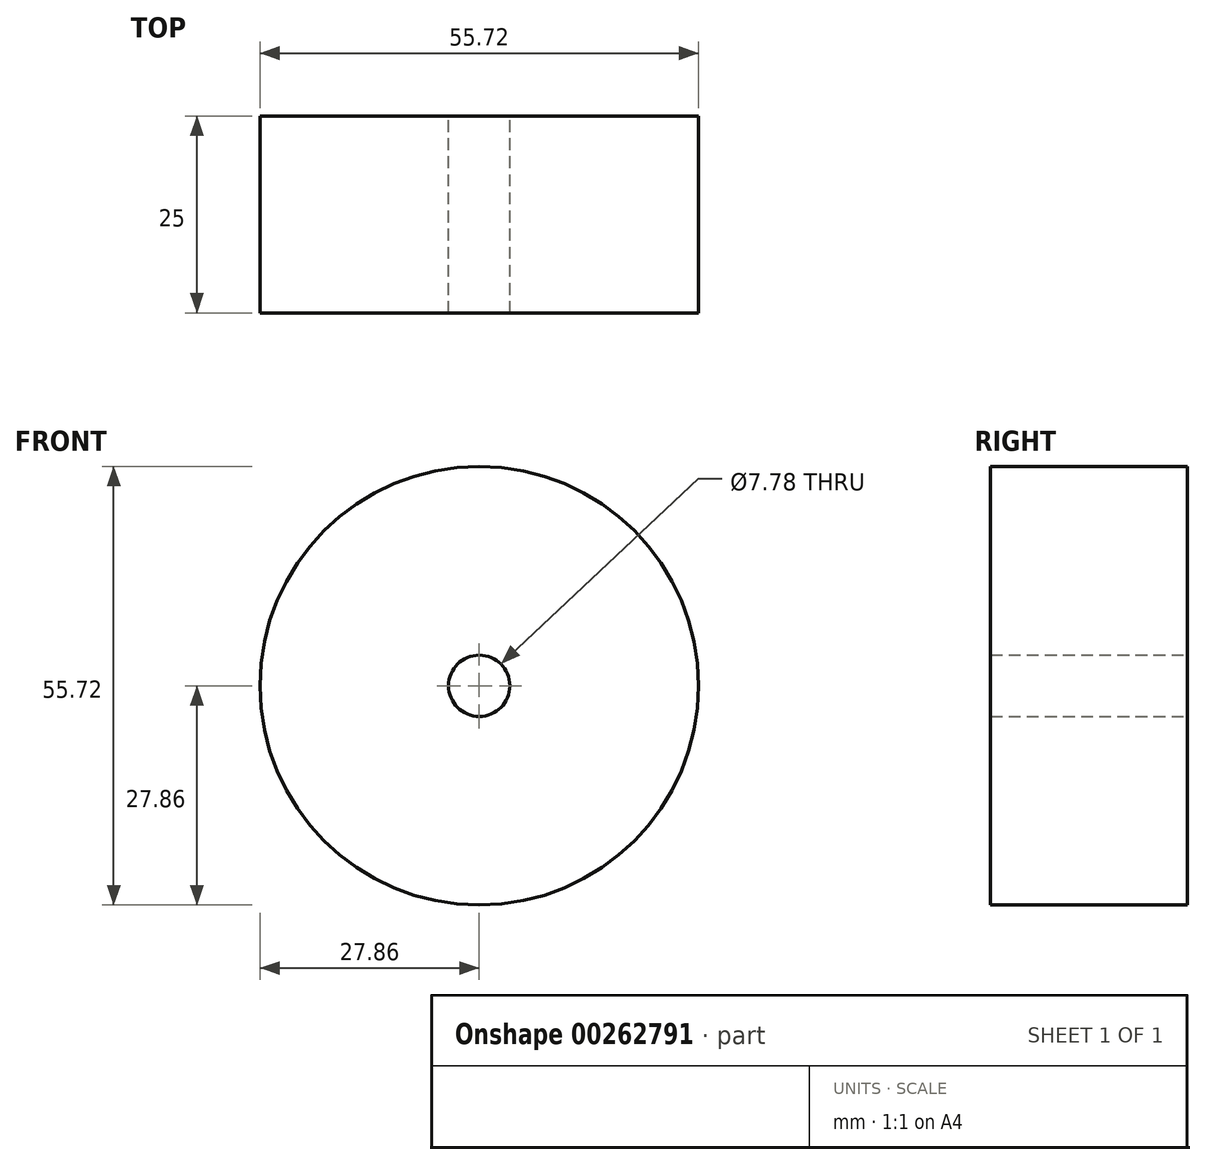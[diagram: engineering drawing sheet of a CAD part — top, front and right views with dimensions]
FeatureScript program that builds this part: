
annotation { "Feature Type Name" : "Feature", "Feature Type Description" : "" }
export const myFeature = defineFeature(function(context is Context, id is Id, definition is map)
    precondition{}
    {
        {
            var Q0;
            Q0=qCreatedBy(makeId("Front.planeOp"),FACE);
            var sketch = newSketch(context, id + "F0", { "sketchPlane" : qUnion([Q0])});
            skCircle(sketch, "E0", {"center": v(0, 0) * mm, "radius": 27.86 * mm});
            skCircle(sketch, "E1", {"center": v(0, 0) * mm, "radius": 3.89 * mm});
            skSolve(sketch);
        }
        {
            var Q0;
            Q0=makeQuery(id+"F0.imprint","IMPRINT",FACE,{"disambiguationData":[TD([[makeQuery(id+"F0.imprint","IMPRINT",EDGE,{"derivedFrom":sQuery(id+"F0.wireOp",EDGE,"E0")}),1.0]])]});
            extrude(context, id + "F1", {"entities" : qUnion([Q0]), "depth" : 25 * mm});
        }
    });
